# Revit family: 2990056 - DLX101 Wash Trough
name_source: partatom
category: Plumbing Fixtures
units: mm (PartAtom-declared; Revit-internal decimal feet)

## family parameters
Always vertical = Yes
Cut with Voids When Loaded = No
OmniClass Number = 23.45.70.00
OmniClass Title = Laundry and Cleaning Equipment
Part Type = Normal
Room Calculation Point = No
Round Connector Dimension = Use Diameter
Shared = No
Work Plane-Based = No

## types (1)
- DLX101 Wash Trough
    Assembly Code = D2010420
    Bowl Dimensions = 540mm x 410mm x 300mm
    CW Connection = No
    Default Elevation = 0 mm  [stored 0 ft]
    Dimensions = 600mm x 440mm x 300mm
    HW Connection = No
    Manufacturer = Franke South Africa (Pty) Ltd
    Material = Grade 430 17/10
    Model = DLX101 Wash trough
    Product Code = 29900056
    Vent Connection = No
    Waste Connection = Yes

note: [stored X ft] marks values corroborated as IEEE doubles in the binary element streams (Revit-internal decimal feet)

## geometry (parser evidence)
native form markers: Blend x6, Sweep x3
no freeform markers — native parametric forms only
